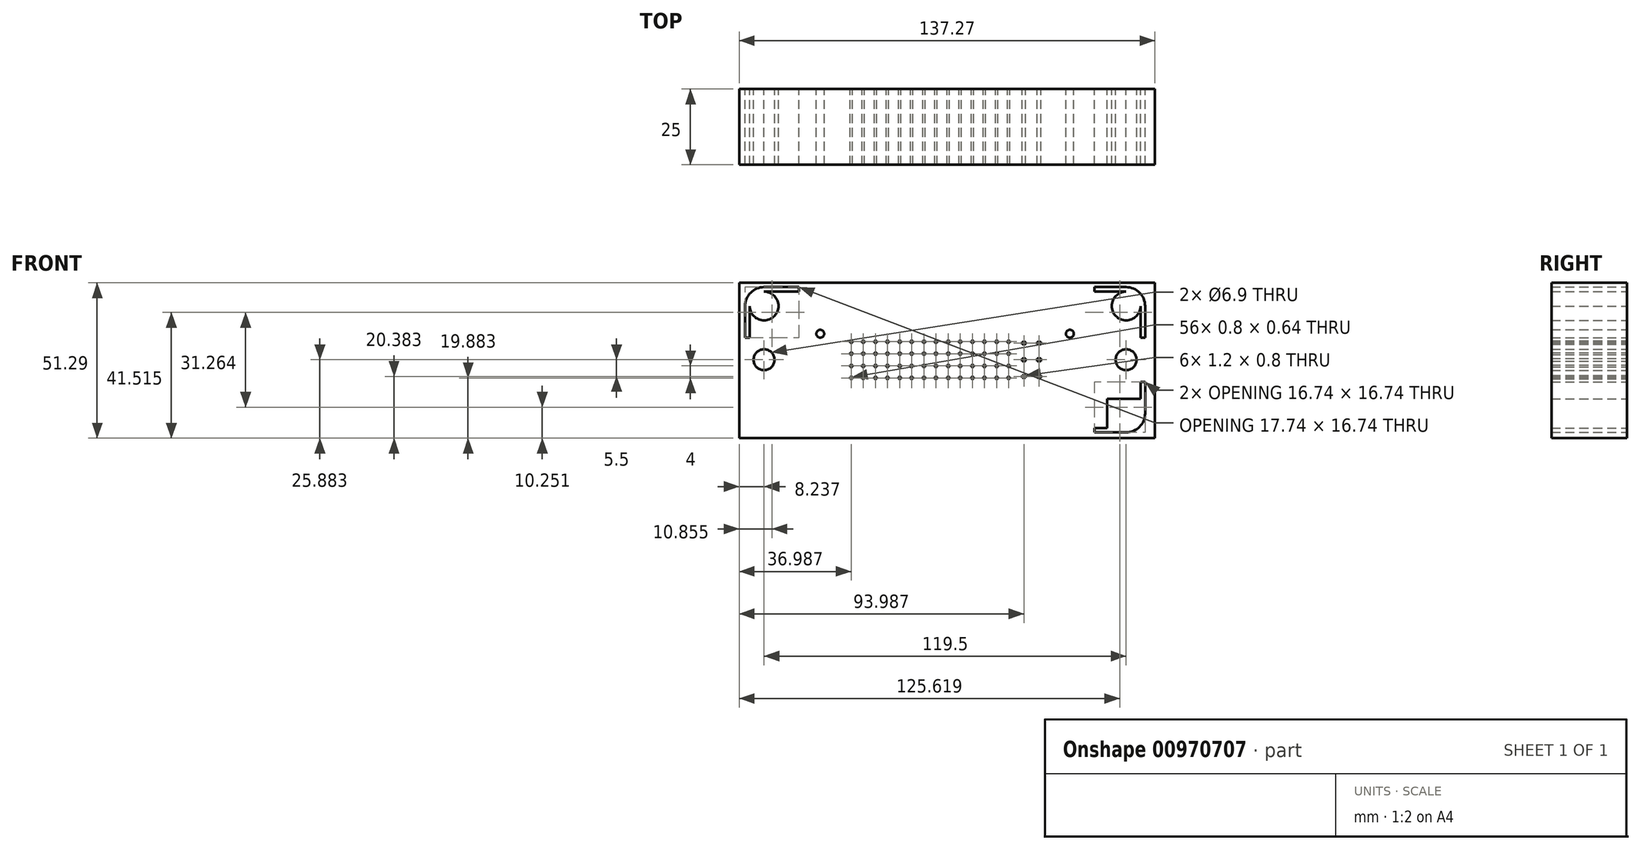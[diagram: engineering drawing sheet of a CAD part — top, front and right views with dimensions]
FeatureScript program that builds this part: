
annotation { "Feature Type Name" : "Feature", "Feature Type Description" : "" }
export const myFeature = defineFeature(function(context is Context, id is Id, definition is map)
    precondition{}
    {
        {
            var Q0;
            Q0=qCreatedBy(makeId("Front.planeOp"),FACE);
            var sketch = newSketch(context, id + "F0", { "sketchPlane" : qUnion([Q0])});
            skFitSpline(sketch, "E0.0", {"points": [v(-52.7, 24.5) * mm, v(-19.86, 24.5) * mm, v(12.98, 24.5) * mm, v(45.82, 24.5) * mm]});
            skPoint(sketch, "E1.0", {"position": v(-52.7, 23.75) * mm});
            skLineSegment(sketch, "E2.0", {"start": v(-52.7, 23) * mm, "end": v(-52.7, 24.5) * mm});
            skLineSegment(sketch, "E3.0", {"start": v(-52.7, -23.5) * mm, "end": v(-52.7, -22) * mm});
            skFitSpline(sketch, "E4.0", {"points": [v(-52.7, -23.5) * mm, v(-19.86, -23.5) * mm, v(12.98, -23.5) * mm, v(45.82, -23.5) * mm]});
            skLineSegment(sketch, "E5.0", {"start": v(45.82, -22) * mm, "end": v(45.82, -23.5) * mm});
            skFitSpline(sketch, "E6.0.0", {"points": [v(-34.84, 6.18) * mm, v(-34.58, 6.18) * mm, v(-34.3, 6.18) * mm, v(-34.04, 6.18) * mm]});
            skFitSpline(sketch, "E6.0.1", {"points": [v(-34.04, 6.18) * mm, v(-34.04, 6.4) * mm, v(-34.04, 6.6) * mm, v(-34.04, 6.82) * mm]});
            skFitSpline(sketch, "E6.0.2", {"points": [v(-34.04, 6.82) * mm, v(-34.3, 6.82) * mm, v(-34.58, 6.82) * mm, v(-34.84, 6.82) * mm]});
            skFitSpline(sketch, "E6.0.3", {"points": [v(-34.84, 6.82) * mm, v(-34.84, 6.6) * mm, v(-34.84, 6.4) * mm, v(-34.84, 6.18) * mm]});
            skFitSpline(sketch, "E7.0.0", {"points": [v(-30.84, 6.18) * mm, v(-30.58, 6.18) * mm, v(-30.3, 6.18) * mm, v(-30.04, 6.18) * mm]});
            skFitSpline(sketch, "E7.0.1", {"points": [v(-30.04, 6.18) * mm, v(-30.04, 6.4) * mm, v(-30.04, 6.6) * mm, v(-30.04, 6.82) * mm]});
            skFitSpline(sketch, "E7.0.2", {"points": [v(-30.04, 6.82) * mm, v(-30.3, 6.82) * mm, v(-30.58, 6.82) * mm, v(-30.84, 6.82) * mm]});
            skFitSpline(sketch, "E7.0.3", {"points": [v(-30.84, 6.82) * mm, v(-30.84, 6.6) * mm, v(-30.84, 6.4) * mm, v(-30.84, 6.18) * mm]});
            skFitSpline(sketch, "E8.0.0", {"points": [v(-26.84, 6.18) * mm, v(-26.58, 6.18) * mm, v(-26.3, 6.18) * mm, v(-26.04, 6.18) * mm]});
            skFitSpline(sketch, "E8.0.1", {"points": [v(-26.04, 6.18) * mm, v(-26.04, 6.4) * mm, v(-26.04, 6.6) * mm, v(-26.04, 6.82) * mm]});
            skFitSpline(sketch, "E8.0.2", {"points": [v(-26.04, 6.82) * mm, v(-26.3, 6.82) * mm, v(-26.58, 6.82) * mm, v(-26.84, 6.82) * mm]});
            skFitSpline(sketch, "E8.0.3", {"points": [v(-26.84, 6.82) * mm, v(-26.84, 6.6) * mm, v(-26.84, 6.4) * mm, v(-26.84, 6.18) * mm]});
            skFitSpline(sketch, "E9.0.0", {"points": [v(-22.84, 6.18) * mm, v(-22.58, 6.18) * mm, v(-22.3, 6.18) * mm, v(-22.04, 6.18) * mm]});
            skFitSpline(sketch, "E9.0.1", {"points": [v(-22.04, 6.18) * mm, v(-22.04, 6.4) * mm, v(-22.04, 6.6) * mm, v(-22.04, 6.82) * mm]});
            skFitSpline(sketch, "E9.0.2", {"points": [v(-22.04, 6.82) * mm, v(-22.3, 6.82) * mm, v(-22.58, 6.82) * mm, v(-22.84, 6.82) * mm]});
            skFitSpline(sketch, "E9.0.3", {"points": [v(-22.84, 6.82) * mm, v(-22.84, 6.6) * mm, v(-22.84, 6.4) * mm, v(-22.84, 6.18) * mm]});
            skFitSpline(sketch, "E10.0.0", {"points": [v(-34.84, 2.18) * mm, v(-34.58, 2.18) * mm, v(-34.3, 2.18) * mm, v(-34.04, 2.18) * mm]});
            skFitSpline(sketch, "E10.0.1", {"points": [v(-34.04, 2.18) * mm, v(-34.04, 2.4) * mm, v(-34.04, 2.6) * mm, v(-34.04, 2.82) * mm]});
            skFitSpline(sketch, "E10.0.2", {"points": [v(-34.04, 2.82) * mm, v(-34.3, 2.82) * mm, v(-34.58, 2.82) * mm, v(-34.84, 2.82) * mm]});
            skFitSpline(sketch, "E10.0.3", {"points": [v(-34.84, 2.82) * mm, v(-34.84, 2.6) * mm, v(-34.84, 2.4) * mm, v(-34.84, 2.18) * mm]});
            skFitSpline(sketch, "E11.0.0", {"points": [v(-30.84, 2.18) * mm, v(-30.58, 2.18) * mm, v(-30.3, 2.18) * mm, v(-30.04, 2.18) * mm]});
            skFitSpline(sketch, "E11.0.1", {"points": [v(-30.04, 2.18) * mm, v(-30.04, 2.4) * mm, v(-30.04, 2.6) * mm, v(-30.04, 2.82) * mm]});
            skFitSpline(sketch, "E11.0.2", {"points": [v(-30.04, 2.82) * mm, v(-30.3, 2.82) * mm, v(-30.58, 2.82) * mm, v(-30.84, 2.82) * mm]});
            skFitSpline(sketch, "E11.0.3", {"points": [v(-30.84, 2.82) * mm, v(-30.84, 2.6) * mm, v(-30.84, 2.4) * mm, v(-30.84, 2.18) * mm]});
            skFitSpline(sketch, "E12.0.0", {"points": [v(-26.84, 2.18) * mm, v(-26.58, 2.18) * mm, v(-26.3, 2.18) * mm, v(-26.04, 2.18) * mm]});
            skFitSpline(sketch, "E12.0.1", {"points": [v(-26.04, 2.18) * mm, v(-26.04, 2.4) * mm, v(-26.04, 2.6) * mm, v(-26.04, 2.82) * mm]});
            skFitSpline(sketch, "E12.0.2", {"points": [v(-26.04, 2.82) * mm, v(-26.3, 2.82) * mm, v(-26.58, 2.82) * mm, v(-26.84, 2.82) * mm]});
            skFitSpline(sketch, "E12.0.3", {"points": [v(-26.84, 2.82) * mm, v(-26.84, 2.6) * mm, v(-26.84, 2.4) * mm, v(-26.84, 2.18) * mm]});
            skFitSpline(sketch, "E13.0.0", {"points": [v(-22.84, 2.18) * mm, v(-22.58, 2.18) * mm, v(-22.3, 2.18) * mm, v(-22.04, 2.18) * mm]});
            skFitSpline(sketch, "E13.0.1", {"points": [v(-22.04, 2.18) * mm, v(-22.04, 2.4) * mm, v(-22.04, 2.6) * mm, v(-22.04, 2.82) * mm]});
            skFitSpline(sketch, "E13.0.2", {"points": [v(-22.04, 2.82) * mm, v(-22.3, 2.82) * mm, v(-22.58, 2.82) * mm, v(-22.84, 2.82) * mm]});
            skFitSpline(sketch, "E13.0.3", {"points": [v(-22.84, 2.82) * mm, v(-22.84, 2.6) * mm, v(-22.84, 2.4) * mm, v(-22.84, 2.18) * mm]});
            skFitSpline(sketch, "E14.0.0", {"points": [v(-18.84, 6.18) * mm, v(-18.58, 6.18) * mm, v(-18.3, 6.18) * mm, v(-18.04, 6.18) * mm]});
            skFitSpline(sketch, "E14.0.1", {"points": [v(-18.04, 6.18) * mm, v(-18.04, 6.4) * mm, v(-18.04, 6.6) * mm, v(-18.04, 6.82) * mm]});
            skFitSpline(sketch, "E14.0.2", {"points": [v(-18.04, 6.82) * mm, v(-18.3, 6.82) * mm, v(-18.58, 6.82) * mm, v(-18.84, 6.82) * mm]});
            skFitSpline(sketch, "E14.0.3", {"points": [v(-18.84, 6.82) * mm, v(-18.84, 6.6) * mm, v(-18.84, 6.4) * mm, v(-18.84, 6.18) * mm]});
            skFitSpline(sketch, "E15.0.0", {"points": [v(-18.84, 2.18) * mm, v(-18.58, 2.18) * mm, v(-18.3, 2.18) * mm, v(-18.04, 2.18) * mm]});
            skFitSpline(sketch, "E15.0.1", {"points": [v(-18.04, 2.18) * mm, v(-18.04, 2.4) * mm, v(-18.04, 2.6) * mm, v(-18.04, 2.82) * mm]});
            skFitSpline(sketch, "E15.0.2", {"points": [v(-18.04, 2.82) * mm, v(-18.3, 2.82) * mm, v(-18.58, 2.82) * mm, v(-18.84, 2.82) * mm]});
            skFitSpline(sketch, "E15.0.3", {"points": [v(-18.84, 2.82) * mm, v(-18.84, 2.6) * mm, v(-18.84, 2.4) * mm, v(-18.84, 2.18) * mm]});
            skFitSpline(sketch, "E16.0.0", {"points": [v(-14.84, 6.18) * mm, v(-14.58, 6.18) * mm, v(-14.3, 6.18) * mm, v(-14.04, 6.18) * mm]});
            skFitSpline(sketch, "E16.0.1", {"points": [v(-14.04, 6.18) * mm, v(-14.04, 6.4) * mm, v(-14.04, 6.6) * mm, v(-14.04, 6.82) * mm]});
            skFitSpline(sketch, "E16.0.2", {"points": [v(-14.04, 6.82) * mm, v(-14.3, 6.82) * mm, v(-14.58, 6.82) * mm, v(-14.84, 6.82) * mm]});
            skFitSpline(sketch, "E16.0.3", {"points": [v(-14.84, 6.82) * mm, v(-14.84, 6.6) * mm, v(-14.84, 6.4) * mm, v(-14.84, 6.18) * mm]});
            skFitSpline(sketch, "E17.0.0", {"points": [v(-14.84, 2.18) * mm, v(-14.58, 2.18) * mm, v(-14.3, 2.18) * mm, v(-14.04, 2.18) * mm]});
            skFitSpline(sketch, "E17.0.1", {"points": [v(-14.04, 2.18) * mm, v(-14.04, 2.4) * mm, v(-14.04, 2.6) * mm, v(-14.04, 2.82) * mm]});
            skFitSpline(sketch, "E17.0.2", {"points": [v(-14.04, 2.82) * mm, v(-14.3, 2.82) * mm, v(-14.58, 2.82) * mm, v(-14.84, 2.82) * mm]});
            skFitSpline(sketch, "E17.0.3", {"points": [v(-14.84, 2.82) * mm, v(-14.84, 2.6) * mm, v(-14.84, 2.4) * mm, v(-14.84, 2.18) * mm]});
            skFitSpline(sketch, "E18.0.0", {"points": [v(-10.84, 6.18) * mm, v(-10.58, 6.18) * mm, v(-10.3, 6.18) * mm, v(-10.04, 6.18) * mm]});
            skFitSpline(sketch, "E18.0.1", {"points": [v(-10.04, 6.18) * mm, v(-10.04, 6.4) * mm, v(-10.04, 6.6) * mm, v(-10.04, 6.82) * mm]});
            skFitSpline(sketch, "E18.0.2", {"points": [v(-10.04, 6.82) * mm, v(-10.3, 6.82) * mm, v(-10.58, 6.82) * mm, v(-10.84, 6.82) * mm]});
            skFitSpline(sketch, "E18.0.3", {"points": [v(-10.84, 6.82) * mm, v(-10.84, 6.6) * mm, v(-10.84, 6.4) * mm, v(-10.84, 6.18) * mm]});
            skFitSpline(sketch, "E19.0.0", {"points": [v(-10.84, 2.18) * mm, v(-10.58, 2.18) * mm, v(-10.3, 2.18) * mm, v(-10.04, 2.18) * mm]});
            skFitSpline(sketch, "E19.0.1", {"points": [v(-10.04, 2.18) * mm, v(-10.04, 2.4) * mm, v(-10.04, 2.6) * mm, v(-10.04, 2.82) * mm]});
            skFitSpline(sketch, "E19.0.2", {"points": [v(-10.04, 2.82) * mm, v(-10.3, 2.82) * mm, v(-10.58, 2.82) * mm, v(-10.84, 2.82) * mm]});
            skFitSpline(sketch, "E19.0.3", {"points": [v(-10.84, 2.82) * mm, v(-10.84, 2.6) * mm, v(-10.84, 2.4) * mm, v(-10.84, 2.18) * mm]});
            skFitSpline(sketch, "E20.0.0", {"points": [v(-6.84, 6.18) * mm, v(-6.58, 6.18) * mm, v(-6.3, 6.18) * mm, v(-6.04, 6.18) * mm]});
            skFitSpline(sketch, "E20.0.1", {"points": [v(-6.04, 6.18) * mm, v(-6.04, 6.4) * mm, v(-6.04, 6.6) * mm, v(-6.04, 6.82) * mm]});
            skFitSpline(sketch, "E20.0.2", {"points": [v(-6.04, 6.82) * mm, v(-6.3, 6.82) * mm, v(-6.58, 6.82) * mm, v(-6.84, 6.82) * mm]});
            skFitSpline(sketch, "E20.0.3", {"points": [v(-6.84, 6.82) * mm, v(-6.84, 6.6) * mm, v(-6.84, 6.4) * mm, v(-6.84, 6.18) * mm]});
            skFitSpline(sketch, "E21.0.0", {"points": [v(-6.84, 2.18) * mm, v(-6.58, 2.18) * mm, v(-6.3, 2.18) * mm, v(-6.04, 2.18) * mm]});
            skFitSpline(sketch, "E21.0.1", {"points": [v(-6.04, 2.18) * mm, v(-6.04, 2.4) * mm, v(-6.04, 2.6) * mm, v(-6.04, 2.82) * mm]});
            skFitSpline(sketch, "E21.0.2", {"points": [v(-6.04, 2.82) * mm, v(-6.3, 2.82) * mm, v(-6.58, 2.82) * mm, v(-6.84, 2.82) * mm]});
            skFitSpline(sketch, "E21.0.3", {"points": [v(-6.84, 2.82) * mm, v(-6.84, 2.6) * mm, v(-6.84, 2.4) * mm, v(-6.84, 2.18) * mm]});
            skFitSpline(sketch, "E22.0.0", {"points": [v(-2.84, 6.18) * mm, v(-2.58, 6.18) * mm, v(-2.3, 6.18) * mm, v(-2.04, 6.18) * mm]});
            skFitSpline(sketch, "E22.0.1", {"points": [v(-2.04, 6.18) * mm, v(-2.04, 6.4) * mm, v(-2.04, 6.6) * mm, v(-2.04, 6.82) * mm]});
            skFitSpline(sketch, "E22.0.2", {"points": [v(-2.04, 6.82) * mm, v(-2.3, 6.82) * mm, v(-2.58, 6.82) * mm, v(-2.84, 6.82) * mm]});
            skFitSpline(sketch, "E22.0.3", {"points": [v(-2.84, 6.82) * mm, v(-2.84, 6.6) * mm, v(-2.84, 6.4) * mm, v(-2.84, 6.18) * mm]});
            skFitSpline(sketch, "E23.0.0", {"points": [v(-2.84, 2.18) * mm, v(-2.58, 2.18) * mm, v(-2.3, 2.18) * mm, v(-2.04, 2.18) * mm]});
            skFitSpline(sketch, "E23.0.1", {"points": [v(-2.04, 2.18) * mm, v(-2.04, 2.4) * mm, v(-2.04, 2.6) * mm, v(-2.04, 2.82) * mm]});
            skFitSpline(sketch, "E23.0.2", {"points": [v(-2.04, 2.82) * mm, v(-2.3, 2.82) * mm, v(-2.58, 2.82) * mm, v(-2.84, 2.82) * mm]});
            skFitSpline(sketch, "E23.0.3", {"points": [v(-2.84, 2.82) * mm, v(-2.84, 2.6) * mm, v(-2.84, 2.4) * mm, v(-2.84, 2.18) * mm]});
            skFitSpline(sketch, "E24.0.0", {"points": [v(-6.84, -1.82) * mm, v(-6.58, -1.82) * mm, v(-6.3, -1.82) * mm, v(-6.04, -1.82) * mm]});
            skFitSpline(sketch, "E24.0.1", {"points": [v(-6.04, -1.82) * mm, v(-6.04, -1.6) * mm, v(-6.04, -1.4) * mm, v(-6.04, -1.18) * mm]});
            skFitSpline(sketch, "E24.0.2", {"points": [v(-6.04, -1.18) * mm, v(-6.3, -1.18) * mm, v(-6.58, -1.18) * mm, v(-6.84, -1.18) * mm]});
            skFitSpline(sketch, "E24.0.3", {"points": [v(-6.84, -1.18) * mm, v(-6.84, -1.4) * mm, v(-6.84, -1.6) * mm, v(-6.84, -1.82) * mm]});
            skFitSpline(sketch, "E25.0.0", {"points": [v(-10.84, -1.82) * mm, v(-10.58, -1.82) * mm, v(-10.3, -1.82) * mm, v(-10.04, -1.82) * mm]});
            skFitSpline(sketch, "E25.0.1", {"points": [v(-10.04, -1.82) * mm, v(-10.04, -1.6) * mm, v(-10.04, -1.4) * mm, v(-10.04, -1.18) * mm]});
            skFitSpline(sketch, "E25.0.2", {"points": [v(-10.04, -1.18) * mm, v(-10.3, -1.18) * mm, v(-10.58, -1.18) * mm, v(-10.84, -1.18) * mm]});
            skFitSpline(sketch, "E25.0.3", {"points": [v(-10.84, -1.18) * mm, v(-10.84, -1.4) * mm, v(-10.84, -1.6) * mm, v(-10.84, -1.82) * mm]});
            skFitSpline(sketch, "E26.0.0", {"points": [v(-14.84, -1.82) * mm, v(-14.58, -1.82) * mm, v(-14.3, -1.82) * mm, v(-14.04, -1.82) * mm]});
            skFitSpline(sketch, "E26.0.1", {"points": [v(-14.04, -1.82) * mm, v(-14.04, -1.6) * mm, v(-14.04, -1.4) * mm, v(-14.04, -1.18) * mm]});
            skFitSpline(sketch, "E26.0.2", {"points": [v(-14.04, -1.18) * mm, v(-14.3, -1.18) * mm, v(-14.58, -1.18) * mm, v(-14.84, -1.18) * mm]});
            skFitSpline(sketch, "E26.0.3", {"points": [v(-14.84, -1.18) * mm, v(-14.84, -1.4) * mm, v(-14.84, -1.6) * mm, v(-14.84, -1.82) * mm]});
            skFitSpline(sketch, "E27.0.0", {"points": [v(-18.84, -1.82) * mm, v(-18.58, -1.82) * mm, v(-18.3, -1.82) * mm, v(-18.04, -1.82) * mm]});
            skFitSpline(sketch, "E27.0.1", {"points": [v(-18.04, -1.82) * mm, v(-18.04, -1.6) * mm, v(-18.04, -1.4) * mm, v(-18.04, -1.18) * mm]});
            skFitSpline(sketch, "E27.0.2", {"points": [v(-18.04, -1.18) * mm, v(-18.3, -1.18) * mm, v(-18.58, -1.18) * mm, v(-18.84, -1.18) * mm]});
            skFitSpline(sketch, "E27.0.3", {"points": [v(-18.84, -1.18) * mm, v(-18.84, -1.4) * mm, v(-18.84, -1.6) * mm, v(-18.84, -1.82) * mm]});
            skFitSpline(sketch, "E28.0.0", {"points": [v(-22.84, -1.82) * mm, v(-22.58, -1.82) * mm, v(-22.3, -1.82) * mm, v(-22.04, -1.82) * mm]});
            skFitSpline(sketch, "E28.0.1", {"points": [v(-22.04, -1.82) * mm, v(-22.04, -1.6) * mm, v(-22.04, -1.4) * mm, v(-22.04, -1.18) * mm]});
            skFitSpline(sketch, "E28.0.2", {"points": [v(-22.04, -1.18) * mm, v(-22.3, -1.18) * mm, v(-22.58, -1.18) * mm, v(-22.84, -1.18) * mm]});
            skFitSpline(sketch, "E28.0.3", {"points": [v(-22.84, -1.18) * mm, v(-22.84, -1.4) * mm, v(-22.84, -1.6) * mm, v(-22.84, -1.82) * mm]});
            skFitSpline(sketch, "E29.0.0", {"points": [v(-2.84, -1.82) * mm, v(-2.58, -1.82) * mm, v(-2.3, -1.82) * mm, v(-2.04, -1.82) * mm]});
            skFitSpline(sketch, "E29.0.1", {"points": [v(-2.04, -1.82) * mm, v(-2.04, -1.6) * mm, v(-2.04, -1.4) * mm, v(-2.04, -1.18) * mm]});
            skFitSpline(sketch, "E29.0.2", {"points": [v(-2.04, -1.18) * mm, v(-2.3, -1.18) * mm, v(-2.58, -1.18) * mm, v(-2.84, -1.18) * mm]});
            skFitSpline(sketch, "E29.0.3", {"points": [v(-2.84, -1.18) * mm, v(-2.84, -1.4) * mm, v(-2.84, -1.6) * mm, v(-2.84, -1.82) * mm]});
            skFitSpline(sketch, "E30.0.0", {"points": [v(1.16, -1.82) * mm, v(1.42, -1.82) * mm, v(1.7, -1.82) * mm, v(1.96, -1.82) * mm]});
            skFitSpline(sketch, "E30.0.1", {"points": [v(1.96, -1.82) * mm, v(1.96, -1.6) * mm, v(1.96, -1.4) * mm, v(1.96, -1.18) * mm]});
            skFitSpline(sketch, "E30.0.2", {"points": [v(1.96, -1.18) * mm, v(1.7, -1.18) * mm, v(1.42, -1.18) * mm, v(1.16, -1.18) * mm]});
            skFitSpline(sketch, "E30.0.3", {"points": [v(1.16, -1.18) * mm, v(1.16, -1.4) * mm, v(1.16, -1.6) * mm, v(1.16, -1.82) * mm]});
            skFitSpline(sketch, "E31.0.0", {"points": [v(1.16, 6.18) * mm, v(1.42, 6.18) * mm, v(1.7, 6.18) * mm, v(1.96, 6.18) * mm]});
            skFitSpline(sketch, "E31.0.1", {"points": [v(1.96, 6.18) * mm, v(1.96, 6.4) * mm, v(1.96, 6.6) * mm, v(1.96, 6.82) * mm]});
            skFitSpline(sketch, "E31.0.2", {"points": [v(1.96, 6.82) * mm, v(1.7, 6.82) * mm, v(1.42, 6.82) * mm, v(1.16, 6.82) * mm]});
            skFitSpline(sketch, "E31.0.3", {"points": [v(1.16, 6.82) * mm, v(1.16, 6.6) * mm, v(1.16, 6.4) * mm, v(1.16, 6.18) * mm]});
            skFitSpline(sketch, "E32.0.0", {"points": [v(1.16, 2.18) * mm, v(1.42, 2.18) * mm, v(1.7, 2.18) * mm, v(1.96, 2.18) * mm]});
            skFitSpline(sketch, "E32.0.1", {"points": [v(1.96, 2.18) * mm, v(1.96, 2.4) * mm, v(1.96, 2.6) * mm, v(1.96, 2.82) * mm]});
            skFitSpline(sketch, "E32.0.2", {"points": [v(1.96, 2.82) * mm, v(1.7, 2.82) * mm, v(1.42, 2.82) * mm, v(1.16, 2.82) * mm]});
            skFitSpline(sketch, "E32.0.3", {"points": [v(1.16, 2.82) * mm, v(1.16, 2.6) * mm, v(1.16, 2.4) * mm, v(1.16, 2.18) * mm]});
            skFitSpline(sketch, "E33.0.0", {"points": [v(5.16, 2.18) * mm, v(5.42, 2.18) * mm, v(5.7, 2.18) * mm, v(5.96, 2.18) * mm]});
            skFitSpline(sketch, "E33.0.1", {"points": [v(5.96, 2.18) * mm, v(5.96, 2.4) * mm, v(5.96, 2.6) * mm, v(5.96, 2.82) * mm]});
            skFitSpline(sketch, "E33.0.2", {"points": [v(5.96, 2.82) * mm, v(5.7, 2.82) * mm, v(5.42, 2.82) * mm, v(5.16, 2.82) * mm]});
            skFitSpline(sketch, "E33.0.3", {"points": [v(5.16, 2.82) * mm, v(5.16, 2.6) * mm, v(5.16, 2.4) * mm, v(5.16, 2.18) * mm]});
            skFitSpline(sketch, "E34.0.0", {"points": [v(5.16, -1.82) * mm, v(5.42, -1.82) * mm, v(5.7, -1.82) * mm, v(5.96, -1.82) * mm]});
            skFitSpline(sketch, "E34.0.1", {"points": [v(5.96, -1.82) * mm, v(5.96, -1.6) * mm, v(5.96, -1.4) * mm, v(5.96, -1.18) * mm]});
            skFitSpline(sketch, "E34.0.2", {"points": [v(5.96, -1.18) * mm, v(5.7, -1.18) * mm, v(5.42, -1.18) * mm, v(5.16, -1.18) * mm]});
            skFitSpline(sketch, "E34.0.3", {"points": [v(5.16, -1.18) * mm, v(5.16, -1.4) * mm, v(5.16, -1.6) * mm, v(5.16, -1.82) * mm]});
            skFitSpline(sketch, "E35.0.0", {"points": [v(5.16, 6.18) * mm, v(5.42, 6.18) * mm, v(5.7, 6.18) * mm, v(5.96, 6.18) * mm]});
            skFitSpline(sketch, "E35.0.1", {"points": [v(5.96, 6.18) * mm, v(5.96, 6.4) * mm, v(5.96, 6.6) * mm, v(5.96, 6.82) * mm]});
            skFitSpline(sketch, "E35.0.2", {"points": [v(5.96, 6.82) * mm, v(5.7, 6.82) * mm, v(5.42, 6.82) * mm, v(5.16, 6.82) * mm]});
            skFitSpline(sketch, "E35.0.3", {"points": [v(5.16, 6.82) * mm, v(5.16, 6.6) * mm, v(5.16, 6.4) * mm, v(5.16, 6.18) * mm]});
            skFitSpline(sketch, "E36.0.0", {"points": [v(9.16, 6.18) * mm, v(9.42, 6.18) * mm, v(9.7, 6.18) * mm, v(9.96, 6.18) * mm]});
            skFitSpline(sketch, "E36.0.1", {"points": [v(9.96, 6.18) * mm, v(9.96, 6.4) * mm, v(9.96, 6.6) * mm, v(9.96, 6.82) * mm]});
            skFitSpline(sketch, "E36.0.2", {"points": [v(9.96, 6.82) * mm, v(9.7, 6.82) * mm, v(9.42, 6.82) * mm, v(9.16, 6.82) * mm]});
            skFitSpline(sketch, "E36.0.3", {"points": [v(9.16, 6.82) * mm, v(9.16, 6.6) * mm, v(9.16, 6.4) * mm, v(9.16, 6.18) * mm]});
            skFitSpline(sketch, "E37.0.0", {"points": [v(9.16, 2.18) * mm, v(9.42, 2.18) * mm, v(9.7, 2.18) * mm, v(9.96, 2.18) * mm]});
            skFitSpline(sketch, "E37.0.1", {"points": [v(9.96, 2.18) * mm, v(9.96, 2.4) * mm, v(9.96, 2.6) * mm, v(9.96, 2.82) * mm]});
            skFitSpline(sketch, "E37.0.2", {"points": [v(9.96, 2.82) * mm, v(9.7, 2.82) * mm, v(9.42, 2.82) * mm, v(9.16, 2.82) * mm]});
            skFitSpline(sketch, "E37.0.3", {"points": [v(9.16, 2.82) * mm, v(9.16, 2.6) * mm, v(9.16, 2.4) * mm, v(9.16, 2.18) * mm]});
            skFitSpline(sketch, "E38.0.0", {"points": [v(9.16, -1.82) * mm, v(9.42, -1.82) * mm, v(9.7, -1.82) * mm, v(9.96, -1.82) * mm]});
            skFitSpline(sketch, "E38.0.1", {"points": [v(9.96, -1.82) * mm, v(9.96, -1.6) * mm, v(9.96, -1.4) * mm, v(9.96, -1.18) * mm]});
            skFitSpline(sketch, "E38.0.2", {"points": [v(9.96, -1.18) * mm, v(9.7, -1.18) * mm, v(9.42, -1.18) * mm, v(9.16, -1.18) * mm]});
            skFitSpline(sketch, "E38.0.3", {"points": [v(9.16, -1.18) * mm, v(9.16, -1.4) * mm, v(9.16, -1.6) * mm, v(9.16, -1.82) * mm]});
            skFitSpline(sketch, "E39.0.0", {"points": [v(13.16, -1.82) * mm, v(13.42, -1.82) * mm, v(13.7, -1.82) * mm, v(13.96, -1.82) * mm]});
            skFitSpline(sketch, "E39.0.1", {"points": [v(13.96, -1.82) * mm, v(13.96, -1.6) * mm, v(13.96, -1.4) * mm, v(13.96, -1.18) * mm]});
            skFitSpline(sketch, "E39.0.2", {"points": [v(13.96, -1.18) * mm, v(13.7, -1.18) * mm, v(13.42, -1.18) * mm, v(13.16, -1.18) * mm]});
            skFitSpline(sketch, "E39.0.3", {"points": [v(13.16, -1.18) * mm, v(13.16, -1.4) * mm, v(13.16, -1.6) * mm, v(13.16, -1.82) * mm]});
            skFitSpline(sketch, "E40.0.0", {"points": [v(13.16, 2.18) * mm, v(13.42, 2.18) * mm, v(13.7, 2.18) * mm, v(13.96, 2.18) * mm]});
            skFitSpline(sketch, "E40.0.1", {"points": [v(13.96, 2.18) * mm, v(13.96, 2.4) * mm, v(13.96, 2.6) * mm, v(13.96, 2.82) * mm]});
            skFitSpline(sketch, "E40.0.2", {"points": [v(13.96, 2.82) * mm, v(13.7, 2.82) * mm, v(13.42, 2.82) * mm, v(13.16, 2.82) * mm]});
            skFitSpline(sketch, "E40.0.3", {"points": [v(13.16, 2.82) * mm, v(13.16, 2.6) * mm, v(13.16, 2.4) * mm, v(13.16, 2.18) * mm]});
            skFitSpline(sketch, "E41.0.0", {"points": [v(13.16, 6.18) * mm, v(13.42, 6.18) * mm, v(13.7, 6.18) * mm, v(13.96, 6.18) * mm]});
            skFitSpline(sketch, "E41.0.1", {"points": [v(13.96, 6.18) * mm, v(13.96, 6.4) * mm, v(13.96, 6.6) * mm, v(13.96, 6.82) * mm]});
            skFitSpline(sketch, "E41.0.2", {"points": [v(13.96, 6.82) * mm, v(13.7, 6.82) * mm, v(13.42, 6.82) * mm, v(13.16, 6.82) * mm]});
            skFitSpline(sketch, "E41.0.3", {"points": [v(13.16, 6.82) * mm, v(13.16, 6.6) * mm, v(13.16, 6.4) * mm, v(13.16, 6.18) * mm]});
            skFitSpline(sketch, "E42.0.0", {"points": [v(17.16, 6.18) * mm, v(17.42, 6.18) * mm, v(17.7, 6.18) * mm, v(17.96, 6.18) * mm]});
            skFitSpline(sketch, "E42.0.1", {"points": [v(17.96, 6.18) * mm, v(17.96, 6.4) * mm, v(17.96, 6.6) * mm, v(17.96, 6.82) * mm]});
            skFitSpline(sketch, "E42.0.2", {"points": [v(17.96, 6.82) * mm, v(17.7, 6.82) * mm, v(17.42, 6.82) * mm, v(17.16, 6.82) * mm]});
            skFitSpline(sketch, "E42.0.3", {"points": [v(17.16, 6.82) * mm, v(17.16, 6.6) * mm, v(17.16, 6.4) * mm, v(17.16, 6.18) * mm]});
            skFitSpline(sketch, "E43.0.0", {"points": [v(21.96, 5.6) * mm, v(22.36, 5.6) * mm, v(22.76, 5.6) * mm, v(23.16, 5.6) * mm]});
            skFitSpline(sketch, "E43.0.1", {"points": [v(23.16, 5.6) * mm, v(23.16, 5.87) * mm, v(23.16, 6.14) * mm, v(23.16, 6.4) * mm]});
            skFitSpline(sketch, "E43.0.2", {"points": [v(23.16, 6.4) * mm, v(22.76, 6.4) * mm, v(22.36, 6.4) * mm, v(21.96, 6.4) * mm]});
            skFitSpline(sketch, "E43.0.3", {"points": [v(21.96, 6.4) * mm, v(21.96, 6.14) * mm, v(21.96, 5.87) * mm, v(21.96, 5.6) * mm]});
            skFitSpline(sketch, "E44.0.0", {"points": [v(17.16, 2.18) * mm, v(17.42, 2.18) * mm, v(17.7, 2.18) * mm, v(17.96, 2.18) * mm]});
            skFitSpline(sketch, "E44.0.1", {"points": [v(17.96, 2.18) * mm, v(17.96, 2.4) * mm, v(17.96, 2.6) * mm, v(17.96, 2.82) * mm]});
            skFitSpline(sketch, "E44.0.2", {"points": [v(17.96, 2.82) * mm, v(17.7, 2.82) * mm, v(17.42, 2.82) * mm, v(17.16, 2.82) * mm]});
            skFitSpline(sketch, "E44.0.3", {"points": [v(17.16, 2.82) * mm, v(17.16, 2.6) * mm, v(17.16, 2.4) * mm, v(17.16, 2.18) * mm]});
            skFitSpline(sketch, "E45.0.0", {"points": [v(17.16, -1.82) * mm, v(17.42, -1.82) * mm, v(17.7, -1.82) * mm, v(17.96, -1.82) * mm]});
            skFitSpline(sketch, "E45.0.1", {"points": [v(17.96, -1.82) * mm, v(17.96, -1.6) * mm, v(17.96, -1.4) * mm, v(17.96, -1.18) * mm]});
            skFitSpline(sketch, "E45.0.2", {"points": [v(17.96, -1.18) * mm, v(17.7, -1.18) * mm, v(17.42, -1.18) * mm, v(17.16, -1.18) * mm]});
            skFitSpline(sketch, "E45.0.3", {"points": [v(17.16, -1.18) * mm, v(17.16, -1.4) * mm, v(17.16, -1.6) * mm, v(17.16, -1.82) * mm]});
            skFitSpline(sketch, "E46.0.0", {"points": [v(17.16, -5.82) * mm, v(17.42, -5.82) * mm, v(17.7, -5.82) * mm, v(17.96, -5.82) * mm]});
            skFitSpline(sketch, "E46.0.1", {"points": [v(17.96, -5.82) * mm, v(17.96, -5.6) * mm, v(17.96, -5.4) * mm, v(17.96, -5.18) * mm]});
            skFitSpline(sketch, "E46.0.2", {"points": [v(17.96, -5.18) * mm, v(17.7, -5.18) * mm, v(17.42, -5.18) * mm, v(17.16, -5.18) * mm]});
            skFitSpline(sketch, "E46.0.3", {"points": [v(17.16, -5.18) * mm, v(17.16, -5.4) * mm, v(17.16, -5.6) * mm, v(17.16, -5.82) * mm]});
            skFitSpline(sketch, "E47.0.0", {"points": [v(13.16, -5.82) * mm, v(13.42, -5.82) * mm, v(13.7, -5.82) * mm, v(13.96, -5.82) * mm]});
            skFitSpline(sketch, "E47.0.1", {"points": [v(13.96, -5.82) * mm, v(13.96, -5.6) * mm, v(13.96, -5.4) * mm, v(13.96, -5.18) * mm]});
            skFitSpline(sketch, "E47.0.2", {"points": [v(13.96, -5.18) * mm, v(13.7, -5.18) * mm, v(13.42, -5.18) * mm, v(13.16, -5.18) * mm]});
            skFitSpline(sketch, "E47.0.3", {"points": [v(13.16, -5.18) * mm, v(13.16, -5.4) * mm, v(13.16, -5.6) * mm, v(13.16, -5.82) * mm]});
            skFitSpline(sketch, "E48.0.0", {"points": [v(9.16, -5.82) * mm, v(9.42, -5.82) * mm, v(9.7, -5.82) * mm, v(9.96, -5.82) * mm]});
            skFitSpline(sketch, "E48.0.1", {"points": [v(9.96, -5.82) * mm, v(9.96, -5.6) * mm, v(9.96, -5.4) * mm, v(9.96, -5.18) * mm]});
            skFitSpline(sketch, "E48.0.2", {"points": [v(9.96, -5.18) * mm, v(9.7, -5.18) * mm, v(9.42, -5.18) * mm, v(9.16, -5.18) * mm]});
            skFitSpline(sketch, "E48.0.3", {"points": [v(9.16, -5.18) * mm, v(9.16, -5.4) * mm, v(9.16, -5.6) * mm, v(9.16, -5.82) * mm]});
            skFitSpline(sketch, "E49.0.0", {"points": [v(5.16, -5.82) * mm, v(5.42, -5.82) * mm, v(5.7, -5.82) * mm, v(5.96, -5.82) * mm]});
            skFitSpline(sketch, "E49.0.1", {"points": [v(5.96, -5.82) * mm, v(5.96, -5.6) * mm, v(5.96, -5.4) * mm, v(5.96, -5.18) * mm]});
            skFitSpline(sketch, "E49.0.2", {"points": [v(5.96, -5.18) * mm, v(5.7, -5.18) * mm, v(5.42, -5.18) * mm, v(5.16, -5.18) * mm]});
            skFitSpline(sketch, "E49.0.3", {"points": [v(5.16, -5.18) * mm, v(5.16, -5.4) * mm, v(5.16, -5.6) * mm, v(5.16, -5.82) * mm]});
            skFitSpline(sketch, "E50.0.0", {"points": [v(1.16, -5.82) * mm, v(1.42, -5.82) * mm, v(1.7, -5.82) * mm, v(1.96, -5.82) * mm]});
            skFitSpline(sketch, "E50.0.1", {"points": [v(1.96, -5.82) * mm, v(1.96, -5.6) * mm, v(1.96, -5.4) * mm, v(1.96, -5.18) * mm]});
            skFitSpline(sketch, "E50.0.2", {"points": [v(1.96, -5.18) * mm, v(1.7, -5.18) * mm, v(1.42, -5.18) * mm, v(1.16, -5.18) * mm]});
            skFitSpline(sketch, "E50.0.3", {"points": [v(1.16, -5.18) * mm, v(1.16, -5.4) * mm, v(1.16, -5.6) * mm, v(1.16, -5.82) * mm]});
            skFitSpline(sketch, "E51.0.0", {"points": [v(-2.84, -5.82) * mm, v(-2.58, -5.82) * mm, v(-2.3, -5.82) * mm, v(-2.04, -5.82) * mm]});
            skFitSpline(sketch, "E51.0.1", {"points": [v(-2.04, -5.82) * mm, v(-2.04, -5.6) * mm, v(-2.04, -5.4) * mm, v(-2.04, -5.18) * mm]});
            skFitSpline(sketch, "E51.0.2", {"points": [v(-2.04, -5.18) * mm, v(-2.3, -5.18) * mm, v(-2.58, -5.18) * mm, v(-2.84, -5.18) * mm]});
            skFitSpline(sketch, "E51.0.3", {"points": [v(-2.84, -5.18) * mm, v(-2.84, -5.4) * mm, v(-2.84, -5.6) * mm, v(-2.84, -5.82) * mm]});
            skFitSpline(sketch, "E52.0.0", {"points": [v(-6.84, -5.82) * mm, v(-6.58, -5.82) * mm, v(-6.3, -5.82) * mm, v(-6.04, -5.82) * mm]});
            skFitSpline(sketch, "E52.0.1", {"points": [v(-6.04, -5.82) * mm, v(-6.04, -5.6) * mm, v(-6.04, -5.4) * mm, v(-6.04, -5.18) * mm]});
            skFitSpline(sketch, "E52.0.2", {"points": [v(-6.04, -5.18) * mm, v(-6.3, -5.18) * mm, v(-6.58, -5.18) * mm, v(-6.84, -5.18) * mm]});
            skFitSpline(sketch, "E52.0.3", {"points": [v(-6.84, -5.18) * mm, v(-6.84, -5.4) * mm, v(-6.84, -5.6) * mm, v(-6.84, -5.82) * mm]});
            skFitSpline(sketch, "E53.0.0", {"points": [v(-10.84, -5.82) * mm, v(-10.58, -5.82) * mm, v(-10.3, -5.82) * mm, v(-10.04, -5.82) * mm]});
            skFitSpline(sketch, "E53.0.1", {"points": [v(-10.04, -5.82) * mm, v(-10.04, -5.6) * mm, v(-10.04, -5.4) * mm, v(-10.04, -5.18) * mm]});
            skFitSpline(sketch, "E53.0.2", {"points": [v(-10.04, -5.18) * mm, v(-10.3, -5.18) * mm, v(-10.58, -5.18) * mm, v(-10.84, -5.18) * mm]});
            skFitSpline(sketch, "E53.0.3", {"points": [v(-10.84, -5.18) * mm, v(-10.84, -5.4) * mm, v(-10.84, -5.6) * mm, v(-10.84, -5.82) * mm]});
            skFitSpline(sketch, "E54.0.0", {"points": [v(-14.84, -5.82) * mm, v(-14.58, -5.82) * mm, v(-14.3, -5.82) * mm, v(-14.04, -5.82) * mm]});
            skFitSpline(sketch, "E54.0.1", {"points": [v(-14.04, -5.82) * mm, v(-14.04, -5.6) * mm, v(-14.04, -5.4) * mm, v(-14.04, -5.18) * mm]});
            skFitSpline(sketch, "E54.0.2", {"points": [v(-14.04, -5.18) * mm, v(-14.3, -5.18) * mm, v(-14.58, -5.18) * mm, v(-14.84, -5.18) * mm]});
            skFitSpline(sketch, "E54.0.3", {"points": [v(-14.84, -5.18) * mm, v(-14.84, -5.4) * mm, v(-14.84, -5.6) * mm, v(-14.84, -5.82) * mm]});
            skFitSpline(sketch, "E55.0.0", {"points": [v(-18.84, -5.82) * mm, v(-18.58, -5.82) * mm, v(-18.3, -5.82) * mm, v(-18.04, -5.82) * mm]});
            skFitSpline(sketch, "E55.0.1", {"points": [v(-18.04, -5.82) * mm, v(-18.04, -5.6) * mm, v(-18.04, -5.4) * mm, v(-18.04, -5.18) * mm]});
            skFitSpline(sketch, "E55.0.2", {"points": [v(-18.04, -5.18) * mm, v(-18.3, -5.18) * mm, v(-18.58, -5.18) * mm, v(-18.84, -5.18) * mm]});
            skFitSpline(sketch, "E55.0.3", {"points": [v(-18.84, -5.18) * mm, v(-18.84, -5.4) * mm, v(-18.84, -5.6) * mm, v(-18.84, -5.82) * mm]});
            skFitSpline(sketch, "E56.0.0", {"points": [v(-22.84, -5.82) * mm, v(-22.58, -5.82) * mm, v(-22.3, -5.82) * mm, v(-22.04, -5.82) * mm]});
            skFitSpline(sketch, "E56.0.1", {"points": [v(-22.04, -5.82) * mm, v(-22.04, -5.6) * mm, v(-22.04, -5.4) * mm, v(-22.04, -5.18) * mm]});
            skFitSpline(sketch, "E56.0.2", {"points": [v(-22.04, -5.18) * mm, v(-22.3, -5.18) * mm, v(-22.58, -5.18) * mm, v(-22.84, -5.18) * mm]});
            skFitSpline(sketch, "E56.0.3", {"points": [v(-22.84, -5.18) * mm, v(-22.84, -5.4) * mm, v(-22.84, -5.6) * mm, v(-22.84, -5.82) * mm]});
            skFitSpline(sketch, "E57.0.0", {"points": [v(-26.84, -1.82) * mm, v(-26.58, -1.82) * mm, v(-26.3, -1.82) * mm, v(-26.04, -1.82) * mm]});
            skFitSpline(sketch, "E57.0.1", {"points": [v(-26.04, -1.82) * mm, v(-26.04, -1.6) * mm, v(-26.04, -1.4) * mm, v(-26.04, -1.18) * mm]});
            skFitSpline(sketch, "E57.0.2", {"points": [v(-26.04, -1.18) * mm, v(-26.3, -1.18) * mm, v(-26.58, -1.18) * mm, v(-26.84, -1.18) * mm]});
            skFitSpline(sketch, "E57.0.3", {"points": [v(-26.84, -1.18) * mm, v(-26.84, -1.4) * mm, v(-26.84, -1.6) * mm, v(-26.84, -1.82) * mm]});
            skFitSpline(sketch, "E58.0.0", {"points": [v(-26.84, -5.82) * mm, v(-26.58, -5.82) * mm, v(-26.3, -5.82) * mm, v(-26.04, -5.82) * mm]});
            skFitSpline(sketch, "E58.0.1", {"points": [v(-26.04, -5.82) * mm, v(-26.04, -5.6) * mm, v(-26.04, -5.4) * mm, v(-26.04, -5.18) * mm]});
            skFitSpline(sketch, "E58.0.2", {"points": [v(-26.04, -5.18) * mm, v(-26.3, -5.18) * mm, v(-26.58, -5.18) * mm, v(-26.84, -5.18) * mm]});
            skFitSpline(sketch, "E58.0.3", {"points": [v(-26.84, -5.18) * mm, v(-26.84, -5.4) * mm, v(-26.84, -5.6) * mm, v(-26.84, -5.82) * mm]});
            skFitSpline(sketch, "E59.0.0", {"points": [v(-30.84, -1.82) * mm, v(-30.58, -1.82) * mm, v(-30.3, -1.82) * mm, v(-30.04, -1.82) * mm]});
            skFitSpline(sketch, "E59.0.1", {"points": [v(-30.04, -1.82) * mm, v(-30.04, -1.6) * mm, v(-30.04, -1.4) * mm, v(-30.04, -1.18) * mm]});
            skFitSpline(sketch, "E59.0.2", {"points": [v(-30.04, -1.18) * mm, v(-30.3, -1.18) * mm, v(-30.58, -1.18) * mm, v(-30.84, -1.18) * mm]});
            skFitSpline(sketch, "E59.0.3", {"points": [v(-30.84, -1.18) * mm, v(-30.84, -1.4) * mm, v(-30.84, -1.6) * mm, v(-30.84, -1.82) * mm]});
            skFitSpline(sketch, "E60.0.0", {"points": [v(-30.84, -5.82) * mm, v(-30.58, -5.82) * mm, v(-30.3, -5.82) * mm, v(-30.04, -5.82) * mm]});
            skFitSpline(sketch, "E60.0.1", {"points": [v(-30.04, -5.82) * mm, v(-30.04, -5.6) * mm, v(-30.04, -5.4) * mm, v(-30.04, -5.18) * mm]});
            skFitSpline(sketch, "E60.0.2", {"points": [v(-30.04, -5.18) * mm, v(-30.3, -5.18) * mm, v(-30.58, -5.18) * mm, v(-30.84, -5.18) * mm]});
            skFitSpline(sketch, "E60.0.3", {"points": [v(-30.84, -5.18) * mm, v(-30.84, -5.4) * mm, v(-30.84, -5.6) * mm, v(-30.84, -5.82) * mm]});
            skFitSpline(sketch, "E61.0.0", {"points": [v(-34.84, -1.82) * mm, v(-34.58, -1.82) * mm, v(-34.3, -1.82) * mm, v(-34.04, -1.82) * mm]});
            skFitSpline(sketch, "E61.0.1", {"points": [v(-34.04, -1.82) * mm, v(-34.04, -1.6) * mm, v(-34.04, -1.4) * mm, v(-34.04, -1.18) * mm]});
            skFitSpline(sketch, "E61.0.2", {"points": [v(-34.04, -1.18) * mm, v(-34.3, -1.18) * mm, v(-34.58, -1.18) * mm, v(-34.84, -1.18) * mm]});
            skFitSpline(sketch, "E61.0.3", {"points": [v(-34.84, -1.18) * mm, v(-34.84, -1.4) * mm, v(-34.84, -1.6) * mm, v(-34.84, -1.82) * mm]});
            skFitSpline(sketch, "E62.0.0", {"points": [v(-34.84, -5.82) * mm, v(-34.58, -5.82) * mm, v(-34.3, -5.82) * mm, v(-34.04, -5.82) * mm]});
            skFitSpline(sketch, "E62.0.1", {"points": [v(-34.04, -5.82) * mm, v(-34.04, -5.6) * mm, v(-34.04, -5.4) * mm, v(-34.04, -5.18) * mm]});
            skFitSpline(sketch, "E62.0.2", {"points": [v(-34.04, -5.18) * mm, v(-34.3, -5.18) * mm, v(-34.58, -5.18) * mm, v(-34.84, -5.18) * mm]});
            skFitSpline(sketch, "E62.0.3", {"points": [v(-34.84, -5.18) * mm, v(-34.84, -5.4) * mm, v(-34.84, -5.6) * mm, v(-34.84, -5.82) * mm]});
            skFitSpline(sketch, "E63.0.0", {"points": [v(26.96, -5.4) * mm, v(27.36, -5.4) * mm, v(27.76, -5.4) * mm, v(28.16, -5.4) * mm]});
            skFitSpline(sketch, "E63.0.1", {"points": [v(28.16, -5.4) * mm, v(28.16, -5.13) * mm, v(28.16, -4.86) * mm, v(28.16, -4.6) * mm]});
            skFitSpline(sketch, "E63.0.2", {"points": [v(28.16, -4.6) * mm, v(27.76, -4.6) * mm, v(27.36, -4.6) * mm, v(26.96, -4.6) * mm]});
            skFitSpline(sketch, "E63.0.3", {"points": [v(26.96, -4.6) * mm, v(26.96, -4.86) * mm, v(26.96, -5.13) * mm, v(26.96, -5.4) * mm]});
            skFitSpline(sketch, "E64.0.0", {"points": [v(26.96, 0.1) * mm, v(27.36, 0.1) * mm, v(27.76, 0.1) * mm, v(28.16, 0.1) * mm]});
            skFitSpline(sketch, "E64.0.1", {"points": [v(28.16, 0.1) * mm, v(28.16, 0.37) * mm, v(28.16, 0.64) * mm, v(28.16, 0.9) * mm]});
            skFitSpline(sketch, "E64.0.2", {"points": [v(28.16, 0.9) * mm, v(27.76, 0.9) * mm, v(27.36, 0.9) * mm, v(26.96, 0.9) * mm]});
            skFitSpline(sketch, "E64.0.3", {"points": [v(26.96, 0.9) * mm, v(26.96, 0.64) * mm, v(26.96, 0.37) * mm, v(26.96, 0.1) * mm]});
            skFitSpline(sketch, "E65.0.0", {"points": [v(26.96, 5.6) * mm, v(27.36, 5.6) * mm, v(27.76, 5.6) * mm, v(28.16, 5.6) * mm]});
            skFitSpline(sketch, "E65.0.1", {"points": [v(28.16, 5.6) * mm, v(28.16, 5.87) * mm, v(28.16, 6.14) * mm, v(28.16, 6.4) * mm]});
            skFitSpline(sketch, "E65.0.2", {"points": [v(28.16, 6.4) * mm, v(27.76, 6.4) * mm, v(27.36, 6.4) * mm, v(26.96, 6.4) * mm]});
            skFitSpline(sketch, "E65.0.3", {"points": [v(26.96, 6.4) * mm, v(26.96, 6.14) * mm, v(26.96, 5.87) * mm, v(26.96, 5.6) * mm]});
            skFitSpline(sketch, "E66.0.0", {"points": [v(21.96, 0.1) * mm, v(22.36, 0.1) * mm, v(22.76, 0.1) * mm, v(23.16, 0.1) * mm]});
            skFitSpline(sketch, "E66.0.1", {"points": [v(23.16, 0.1) * mm, v(23.16, 0.37) * mm, v(23.16, 0.64) * mm, v(23.16, 0.9) * mm]});
            skFitSpline(sketch, "E66.0.2", {"points": [v(23.16, 0.9) * mm, v(22.76, 0.9) * mm, v(22.36, 0.9) * mm, v(21.96, 0.9) * mm]});
            skFitSpline(sketch, "E66.0.3", {"points": [v(21.96, 0.9) * mm, v(21.96, 0.64) * mm, v(21.96, 0.37) * mm, v(21.96, 0.1) * mm]});
            skFitSpline(sketch, "E67.0.0", {"points": [v(21.96, -5.4) * mm, v(22.36, -5.4) * mm, v(22.76, -5.4) * mm, v(23.16, -5.4) * mm]});
            skFitSpline(sketch, "E67.0.1", {"points": [v(23.16, -5.4) * mm, v(23.16, -5.13) * mm, v(23.16, -4.86) * mm, v(23.16, -4.6) * mm]});
            skFitSpline(sketch, "E67.0.2", {"points": [v(23.16, -4.6) * mm, v(22.76, -4.6) * mm, v(22.36, -4.6) * mm, v(21.96, -4.6) * mm]});
            skFitSpline(sketch, "E67.0.3", {"points": [v(21.96, -4.6) * mm, v(21.96, -4.86) * mm, v(21.96, -5.13) * mm, v(21.96, -5.4) * mm]});
            skArc(sketch, "E68.0.0", {"start": v(36.96, 9.1) * mm, "mid": v(37.76, 8.3) * mm, "end": v(38.56, 9.1) * mm});
            skArc(sketch, "E68.0.1", {"start": v(38.56, 9.1) * mm, "mid": v(37.76, 9.9) * mm, "end": v(36.96, 9.1) * mm});
            skArc(sketch, "E69.0.0", {"start": v(-45.44, 9.1) * mm, "mid": v(-44.64, 8.3) * mm, "end": v(-43.84, 9.1) * mm});
            skArc(sketch, "E69.0.1", {"start": v(-43.84, 9.1) * mm, "mid": v(-44.64, 9.9) * mm, "end": v(-45.44, 9.1) * mm});
            skLineSegment(sketch, "E70", {"start": v(-52.7, 23) * mm, "end": v(-51.7, 23) * mm});
            skLineSegment(sketch, "E71", {"start": v(-51.7, 23) * mm, "end": v(-51.7, 25.91) * mm});
            skLineSegment(sketch, "E72", {"start": v(45.82, 23) * mm, "end": v(44.82, 23) * mm});
            skLineSegment(sketch, "E73", {"start": v(-52.7, -23.5) * mm, "end": v(-51.7, -23.5) * mm});
            skLineSegment(sketch, "E74", {"start": v(45.82, -23.5) * mm, "end": v(44.82, -23.5) * mm});
            skLineSegment(sketch, "E75.0", {"start": v(-56.94, 24.5) * mm, "end": v(-52.7, 24.5) * mm});
            skFitSpline(sketch, "E76.0", {"points": [v(-58.36, 24.5) * mm, v(-57.88, 24.5) * mm, v(-57.41, 24.5) * mm, v(-56.94, 24.5) * mm]});
            skLineSegment(sketch, "E77.0", {"start": v(-62.59, 24.5) * mm, "end": v(-58.36, 24.5) * mm});
            skArc(sketch, "E78.0", {"start": v(-63.2, 24.5) * mm, "mid": v(-67.61, 22.67) * mm, "end": v(-69.44, 18.25) * mm});
            skArc(sketch, "E79.0", {"start": v(-67.94, 18.25) * mm, "mid": v(-59.83, 14.9) * mm, "end": v(-63.2, 23) * mm});
            skLineSegment(sketch, "E80.0", {"start": v(-69.44, 12) * mm, "end": v(-69.44, 7.77) * mm});
            skLineSegment(sketch, "E81", {"start": v(-69.44, 13.42) * mm, "end": v(-69.44, 18.25) * mm});
            skLineSegment(sketch, "E82", {"start": v(-62.59, 24.5) * mm, "end": v(-63.2, 24.5) * mm});
            skLineSegment(sketch, "E83", {"start": v(-69.44, 7.77) * mm, "end": v(-67.94, 7.77) * mm});
            skLineSegment(sketch, "E84", {"start": v(-67.94, 7.77) * mm, "end": v(-67.94, 18.25) * mm});
            skLineSegment(sketch, "E85", {"start": v(-51.7, 25.91) * mm, "end": v(-71.43, 25.91) * mm});
            skLineSegment(sketch, "E86", {"start": v(-71.43, 25.91) * mm, "end": v(-71.43, 7.77) * mm});
            skLineSegment(sketch, "E87", {"start": v(-69.44, 13.42) * mm, "end": v(-69.44, 12) * mm});
            skLineSegment(sketch, "E88.0", {"start": v(-69.44, -16.64) * mm, "end": v(-69.44, -12.41) * mm});
            skFitSpline(sketch, "E89.0", {"points": [v(-69.44, -12.41) * mm, v(-69.44, -11.94) * mm, v(-69.44, -11.46) * mm, v(-69.44, -11) * mm]});
            skLineSegment(sketch, "E90.0", {"start": v(-69.44, -11) * mm, "end": v(-69.44, -6.76) * mm});
            skLineSegment(sketch, "E91.0", {"start": v(-67.94, -11) * mm, "end": v(-67.94, -6.76) * mm});
            skFitSpline(sketch, "E92.0", {"points": [v(-67.94, -12.41) * mm, v(-67.94, -11.94) * mm, v(-67.94, -11.46) * mm, v(-67.94, -11) * mm]});
            skLineSegment(sketch, "E93.0", {"start": v(-67.94, -16.64) * mm, "end": v(-67.94, -12.41) * mm});
            skArc(sketch, "E94.0", {"start": v(-63.2, -22) * mm, "mid": v(-59.83, -13.89) * mm, "end": v(-67.94, -17.25) * mm});
            skArc(sketch, "E95.0", {"start": v(-69.44, -17.25) * mm, "mid": v(-67.61, -21.67) * mm, "end": v(-63.2, -23.5) * mm});
            skFitSpline(sketch, "E96.0", {"points": [v(-52.7, -22) * mm, v(-56.2, -22) * mm, v(-59.7, -22) * mm, v(-63.2, -22) * mm]});
            skLineSegment(sketch, "E97.0", {"start": v(-56.94, -23.5) * mm, "end": v(-52.7, -23.5) * mm});
            skFitSpline(sketch, "E98.0", {"points": [v(-58.36, -23.5) * mm, v(-57.88, -23.5) * mm, v(-57.41, -23.5) * mm, v(-56.94, -23.5) * mm]});
            skLineSegment(sketch, "E99.0", {"start": v(-62.59, -23.5) * mm, "end": v(-58.36, -23.5) * mm});
            skLineSegment(sketch, "E100", {"start": v(-62.59, -23.5) * mm, "end": v(-63.2, -23.5) * mm});
            skLineSegment(sketch, "E101.0.1", {"start": v(45.82, 24.5) * mm, "end": v(45.82, 23) * mm});
            skFitSpline(sketch, "E101.0.2", {"points": [v(45.82, 24.5) * mm, v(12.98, 24.5) * mm, v(-19.86, 24.5) * mm, v(-52.7, 24.5) * mm]});
            skLineSegment(sketch, "E101.0.3", {"start": v(-52.7, 24.5) * mm, "end": v(-52.7, 23) * mm});
            skFitSpline(sketch, "E101.0.4", {"points": [v(-52.7, 23) * mm, v(-56.2, 23) * mm, v(-59.7, 23) * mm, v(-63.2, 23) * mm]});
            skArc(sketch, "E101.0.5", {"start": v(-63.2, 23) * mm, "mid": v(-59.83, 14.9) * mm, "end": v(-67.94, 18.25) * mm});
            skFitSpline(sketch, "E101.0.6", {"points": [v(-67.94, 18.25) * mm, v(-67.94, 14.76) * mm, v(-67.94, 11.26) * mm, v(-67.94, 7.77) * mm]});
            skFitSpline(sketch, "E101.0.8", {"points": [v(-69.44, 7.77) * mm, v(-69.44, 2.92) * mm, v(-69.44, -1.92) * mm, v(-69.44, -6.76) * mm]});
            skLineSegment(sketch, "E101.0.9", {"start": v(-69.44, -6.76) * mm, "end": v(-67.94, -6.76) * mm});
            skFitSpline(sketch, "E101.0.10", {"points": [v(-67.94, -6.76) * mm, v(-67.94, -10.26) * mm, v(-67.94, -13.75) * mm, v(-67.94, -17.25) * mm]});
            skArc(sketch, "E101.0.11", {"start": v(-67.94, -17.25) * mm, "mid": v(-59.83, -13.89) * mm, "end": v(-63.2, -22) * mm});
            skFitSpline(sketch, "E101.0.12", {"points": [v(-63.2, -22) * mm, v(-59.7, -22) * mm, v(-56.2, -22) * mm, v(-52.7, -22) * mm]});
            skLineSegment(sketch, "E101.0.13", {"start": v(-52.7, -22) * mm, "end": v(-52.7, -23.5) * mm});
            skFitSpline(sketch, "E101.0.14", {"points": [v(-52.7, -23.5) * mm, v(-19.86, -23.5) * mm, v(12.98, -23.5) * mm, v(45.82, -23.5) * mm]});
            skLineSegment(sketch, "E101.0.19", {"start": v(61.06, -6.76) * mm, "end": v(62.56, -6.76) * mm});
            skFitSpline(sketch, "E101.0.20", {"points": [v(62.56, -6.76) * mm, v(62.56, -1.92) * mm, v(62.56, 2.92) * mm, v(62.56, 7.77) * mm]});
            skLineSegment(sketch, "E101.0.21", {"start": v(61.06, 7.77) * mm, "end": v(62.56, 7.77) * mm});
            skFitSpline(sketch, "E101.0.22", {"points": [v(61.06, 7.77) * mm, v(61.06, 11.26) * mm, v(61.06, 14.76) * mm, v(61.06, 18.25) * mm]});
            skArc(sketch, "E101.0.23", {"start": v(61.06, 18.25) * mm, "mid": v(52.95, 14.9) * mm, "end": v(56.3, 23) * mm});
            skLineSegment(sketch, "E102.0.0", {"start": v(55.7, 24.5) * mm, "end": v(55.7, 23) * mm});
            skFitSpline(sketch, "E102.0.1", {"points": [v(55.7, 23) * mm, v(55.9, 23) * mm, v(56.1, 23) * mm, v(56.3, 23) * mm]});
            skArc(sketch, "E102.0.2", {"start": v(56.3, 23) * mm, "mid": v(52.95, 14.9) * mm, "end": v(61.06, 18.25) * mm});
            skFitSpline(sketch, "E102.0.3", {"points": [v(61.06, 18.25) * mm, v(61.06, 18.05) * mm, v(61.06, 17.85) * mm, v(61.06, 17.65) * mm]});
            skLineSegment(sketch, "E102.0.4", {"start": v(61.06, 17.65) * mm, "end": v(62.56, 17.65) * mm});
            skFitSpline(sketch, "E102.0.5", {"points": [v(62.56, 17.65) * mm, v(62.56, 17.85) * mm, v(62.56, 18.05) * mm, v(62.56, 18.25) * mm]});
            skArc(sketch, "E102.0.6", {"start": v(62.56, 18.25) * mm, "mid": v(60.73, 22.67) * mm, "end": v(56.3, 24.5) * mm});
            skFitSpline(sketch, "E102.0.7", {"points": [v(56.3, 24.5) * mm, v(56.1, 24.5) * mm, v(55.9, 24.5) * mm, v(55.7, 24.5) * mm]});
            skLineSegment(sketch, "E103.0.0", {"start": v(45.82, 24.5) * mm, "end": v(50.05, 24.5) * mm});
            skLineSegment(sketch, "E103.0.2", {"start": v(45.82, 23) * mm, "end": v(50.05, 23) * mm});
            skLineSegment(sketch, "E103.0.3", {"start": v(50.05, 24.5) * mm, "end": v(50.05, 23) * mm});
            skLineSegment(sketch, "E104.0.0", {"start": v(55.7, 24.5) * mm, "end": v(51.47, 24.5) * mm});
            skLineSegment(sketch, "E104.0.1", {"start": v(51.47, 24.5) * mm, "end": v(51.47, 23) * mm});
            skLineSegment(sketch, "E104.0.2", {"start": v(55.7, 23) * mm, "end": v(51.47, 23) * mm});
            skFitSpline(sketch, "E105.0.0", {"points": [v(51.47, 24.5) * mm, v(51, 24.5) * mm, v(50.52, 24.5) * mm, v(50.05, 24.5) * mm]});
            skFitSpline(sketch, "E105.0.2", {"points": [v(50.05, 23) * mm, v(50.52, 23) * mm, v(51, 23) * mm, v(51.47, 23) * mm]});
            skLineSegment(sketch, "E105.0.3", {"start": v(51.47, 23) * mm, "end": v(51.47, 24.5) * mm});
            skLineSegment(sketch, "E106.0.0", {"start": v(62.56, 17.65) * mm, "end": v(62.56, 13.42) * mm});
            skLineSegment(sketch, "E106.0.1", {"start": v(62.56, 17.65) * mm, "end": v(61.06, 17.65) * mm});
            skLineSegment(sketch, "E106.0.2", {"start": v(61.06, 17.65) * mm, "end": v(61.06, 13.42) * mm});
            skLineSegment(sketch, "E106.0.3", {"start": v(61.06, 13.42) * mm, "end": v(62.56, 13.42) * mm});
            skFitSpline(sketch, "E107.0.0", {"points": [v(62.56, 12) * mm, v(62.56, 12.47) * mm, v(62.56, 12.94) * mm, v(62.56, 13.42) * mm]});
            skLineSegment(sketch, "E107.0.1", {"start": v(62.56, 13.42) * mm, "end": v(61.06, 13.42) * mm});
            skFitSpline(sketch, "E107.0.2", {"points": [v(61.06, 13.42) * mm, v(61.06, 12.94) * mm, v(61.06, 12.47) * mm, v(61.06, 12) * mm]});
            skLineSegment(sketch, "E107.0.3", {"start": v(61.06, 12) * mm, "end": v(62.56, 12) * mm});
            skLineSegment(sketch, "E108.0.0", {"start": v(62.56, 7.77) * mm, "end": v(62.56, 12) * mm});
            skLineSegment(sketch, "E108.0.1", {"start": v(62.56, 12) * mm, "end": v(61.06, 12) * mm});
            skLineSegment(sketch, "E108.0.2", {"start": v(61.06, 12) * mm, "end": v(61.06, 7.77) * mm});
            skLineSegment(sketch, "E109.0.1", {"start": v(62.56, -6.76) * mm, "end": v(61.06, -6.76) * mm});
            skArc(sketch, "E110.0.6", {"start": v(56.3, -23.5) * mm, "mid": v(60.73, -21.67) * mm, "end": v(62.56, -17.25) * mm});
            skPoint(sketch, "E111.0", {"position": v(-39.34, 0.5) * mm});
            skFitSpline(sketch, "E112.0", {"points": [v(-34.94, 13.4) * mm, v(-13.94, 13.4) * mm, v(7.06, 13.4) * mm, v(28.06, 13.4) * mm]});
            skArc(sketch, "E113.0", {"start": v(-37.3, 13.02) * mm, "mid": v(-36.14, 13.3) * mm, "end": v(-34.94, 13.4) * mm});
            skFitSpline(sketch, "E114.0.0", {"points": [v(56.3, 23) * mm, v(52.81, 23) * mm, v(49.32, 23) * mm, v(45.82, 23) * mm]});
            skFitSpline(sketch, "E114.0.2", {"points": [v(45.82, 24.5) * mm, v(12.98, 24.5) * mm, v(-19.86, 24.5) * mm, v(-52.7, 24.5) * mm]});
            skFitSpline(sketch, "E114.0.4", {"points": [v(-52.7, 23) * mm, v(-56.2, 23) * mm, v(-59.7, 23) * mm, v(-63.2, 23) * mm]});
            skFitSpline(sketch, "E114.0.6", {"points": [v(-67.94, 18.25) * mm, v(-67.94, 14.76) * mm, v(-67.94, 11.26) * mm, v(-67.94, 7.77) * mm]});
            skFitSpline(sketch, "E114.0.8", {"points": [v(-69.44, 7.77) * mm, v(-69.44, 2.92) * mm, v(-69.44, -1.92) * mm, v(-69.44, -6.76) * mm]});
            skFitSpline(sketch, "E114.0.10", {"points": [v(-67.94, -6.76) * mm, v(-67.94, -10.26) * mm, v(-67.94, -13.75) * mm, v(-67.94, -17.25) * mm]});
            skFitSpline(sketch, "E114.0.12", {"points": [v(-63.2, -22) * mm, v(-59.7, -22) * mm, v(-56.2, -22) * mm, v(-52.7, -22) * mm]});
            skFitSpline(sketch, "E114.0.14", {"points": [v(-52.7, -23.5) * mm, v(-19.86, -23.5) * mm, v(12.98, -23.5) * mm, v(45.82, -23.5) * mm]});
            skFitSpline(sketch, "E114.0.20", {"points": [v(62.56, -6.76) * mm, v(62.56, -1.92) * mm, v(62.56, 2.92) * mm, v(62.56, 7.77) * mm]});
            skFitSpline(sketch, "E114.0.22", {"points": [v(61.06, 7.77) * mm, v(61.06, 11.26) * mm, v(61.06, 14.76) * mm, v(61.06, 18.25) * mm]});
            skArc(sketch, "E115.0", {"start": v(-39.34, 10.17) * mm, "mid": v(-38.78, 11.93) * mm, "end": v(-37.3, 13.02) * mm});
            skFitSpline(sketch, "E116.0", {"points": [v(-39.34, -9.17) * mm, v(-39.34, -2.72) * mm, v(-39.34, 3.73) * mm, v(-39.34, 10.17) * mm]});
            skFitSpline(sketch, "E117.0", {"points": [v(-39.34, -9.17) * mm, v(-39.34, -2.72) * mm, v(-39.34, 3.73) * mm, v(-39.34, 10.17) * mm]});
            skArc(sketch, "E118.0", {"start": v(-37.3, -12.01) * mm, "mid": v(-38.78, -10.92) * mm, "end": v(-39.34, -9.17) * mm});
            skArc(sketch, "E119.0", {"start": v(-34.94, -12.4) * mm, "mid": v(-36.14, -12.3) * mm, "end": v(-37.3, -12.01) * mm});
            skFitSpline(sketch, "E120.0", {"points": [v(28.06, -12.4) * mm, v(7.06, -12.4) * mm, v(-13.94, -12.4) * mm, v(-34.94, -12.4) * mm]});
            skArc(sketch, "E121.0", {"start": v(32.46, -9.17) * mm, "mid": v(31.9, -10.92) * mm, "end": v(30.41, -12.01) * mm});
            skArc(sketch, "E122.0", {"start": v(30.41, -12.01) * mm, "mid": v(29.25, -12.3) * mm, "end": v(28.06, -12.4) * mm});
            skFitSpline(sketch, "E123.0", {"points": [v(32.46, 10.17) * mm, v(32.46, 3.73) * mm, v(32.46, -2.72) * mm, v(32.46, -9.17) * mm]});
            skArc(sketch, "E124.0", {"start": v(30.41, 13.02) * mm, "mid": v(31.9, 11.93) * mm, "end": v(32.46, 10.17) * mm});
            skPoint(sketch, "E125.0", {"position": v(29.25, 13.3) * mm});
            skArc(sketch, "E126.0", {"start": v(-59.74, 0.5) * mm, "mid": v(-63.2, -2.95) * mm, "end": v(-66.64, 0.5) * mm});
            skArc(sketch, "E127.0", {"start": v(-66.64, 0.5) * mm, "mid": v(-63.2, 3.95) * mm, "end": v(-59.74, 0.5) * mm});
            skArc(sketch, "E128.0", {"start": v(52.86, 0.5) * mm, "mid": v(56.3, -2.95) * mm, "end": v(59.76, 0.5) * mm});
            skArc(sketch, "E129.0", {"start": v(59.76, 0.5) * mm, "mid": v(56.3, 3.95) * mm, "end": v(52.86, 0.5) * mm});
            skArc(sketch, "E130.0", {"start": v(36.46, 9.1) * mm, "mid": v(37.76, 7.8) * mm, "end": v(39.06, 9.1) * mm});
            skArc(sketch, "E131.0", {"start": v(39.06, 9.1) * mm, "mid": v(37.76, 10.4) * mm, "end": v(36.46, 9.1) * mm});
            skArc(sketch, "E132.0", {"start": v(36.46, 9.1) * mm, "mid": v(37.76, 10.4) * mm, "end": v(39.06, 9.1) * mm});
            skArc(sketch, "E133.0", {"start": v(-43.34, 9.1) * mm, "mid": v(-44.64, 10.4) * mm, "end": v(-45.94, 9.1) * mm});
            skArc(sketch, "E134.0", {"start": v(-43.34, 9.1) * mm, "mid": v(-44.64, 7.8) * mm, "end": v(-45.94, 9.1) * mm});
            skFitSpline(sketch, "E135.0.0", {"points": [v(56.3, 23) * mm, v(52.81, 23) * mm, v(49.32, 23) * mm, v(45.82, 23) * mm]});
            skFitSpline(sketch, "E135.0.2", {"points": [v(45.82, 24.5) * mm, v(12.98, 24.5) * mm, v(-19.86, 24.5) * mm, v(-52.7, 24.5) * mm]});
            skFitSpline(sketch, "E135.0.4", {"points": [v(-52.7, 23) * mm, v(-56.2, 23) * mm, v(-59.7, 23) * mm, v(-63.2, 23) * mm]});
            skFitSpline(sketch, "E135.0.6", {"points": [v(-67.94, 18.25) * mm, v(-67.94, 14.76) * mm, v(-67.94, 11.26) * mm, v(-67.94, 7.77) * mm]});
            skFitSpline(sketch, "E135.0.8", {"points": [v(-69.44, 7.77) * mm, v(-69.44, 2.92) * mm, v(-69.44, -1.92) * mm, v(-69.44, -6.76) * mm]});
            skFitSpline(sketch, "E135.0.10", {"points": [v(-67.94, -6.76) * mm, v(-67.94, -10.26) * mm, v(-67.94, -13.75) * mm, v(-67.94, -17.25) * mm]});
            skFitSpline(sketch, "E135.0.12", {"points": [v(-63.2, -22) * mm, v(-59.7, -22) * mm, v(-56.2, -22) * mm, v(-52.7, -22) * mm]});
            skFitSpline(sketch, "E135.0.14", {"points": [v(-52.7, -23.5) * mm, v(-19.86, -23.5) * mm, v(12.98, -23.5) * mm, v(45.82, -23.5) * mm]});
            skFitSpline(sketch, "E135.0.20", {"points": [v(62.56, -6.76) * mm, v(62.56, -1.92) * mm, v(62.56, 2.92) * mm, v(62.56, 7.77) * mm]});
            skFitSpline(sketch, "E135.0.22", {"points": [v(61.06, 7.77) * mm, v(61.06, 11.26) * mm, v(61.06, 14.76) * mm, v(61.06, 18.25) * mm]});
            skLineSegment(sketch, "E136", {"start": v(-71.43, 7.77) * mm, "end": v(-71.43, -25.38) * mm});
            skLineSegment(sketch, "E137", {"start": v(-71.43, -25.38) * mm, "end": v(65.84, -25.38) * mm});
            skLineSegment(sketch, "E138", {"start": v(65.84, -25.38) * mm, "end": v(65.84, 25.91) * mm});
            skLineSegment(sketch, "E139", {"start": v(65.84, 25.91) * mm, "end": v(-51.7, 25.91) * mm});
            skLineSegment(sketch, "E140", {"start": v(51.1, -12.41) * mm, "end": v(50.05, -12.41) * mm});
            skLineSegment(sketch, "E141", {"start": v(50.05, -12.41) * mm, "end": v(50.05, -22) * mm});
            skLineSegment(sketch, "E142", {"start": v(51.1, -12.41) * mm, "end": v(61.06, -12.41) * mm});
            skLineSegment(sketch, "E143", {"start": v(45.82, -23.5) * mm, "end": v(56.3, -23.5) * mm});
            skLineSegment(sketch, "E144", {"start": v(62.56, -6.76) * mm, "end": v(62.56, -17.25) * mm});
            skLineSegment(sketch, "E145", {"start": v(61.06, -6.76) * mm, "end": v(61.06, -12.41) * mm});
            skLineSegment(sketch, "E146", {"start": v(50.05, -22) * mm, "end": v(45.82, -22) * mm});
            skSolve(sketch);
        }
        {
            var Q0;
            Q0=makeQuery(id+"F0.imprint","IMPRINT",FACE,{"disambiguationData":[TD([[makeQuery(id+"F0.imprint","IMPRINT",EDGE,{"derivedFrom":sQuery(id+"F0.wireOp",EDGE,"E6.0.0")}),-1.0]])]});
            var Q1;
            {var subQ1=sQuery(id+"F0.wireOp",EDGE,"E75.0");Q1=makeQuery(id+"F0.imprint","IMPRINT",FACE,{"disambiguationData":[TD([[makeQuery(id+"F0.imprint","IMPRINT",EDGE,{"derivedFrom":subQ1}),1.0]])]});}
            extrude(context, id + "F1", {"entities" : qUnion([Q0, Q1]), "depth" : 25 * mm, "offsetDistance" : 25 * mm});
        }
    });
